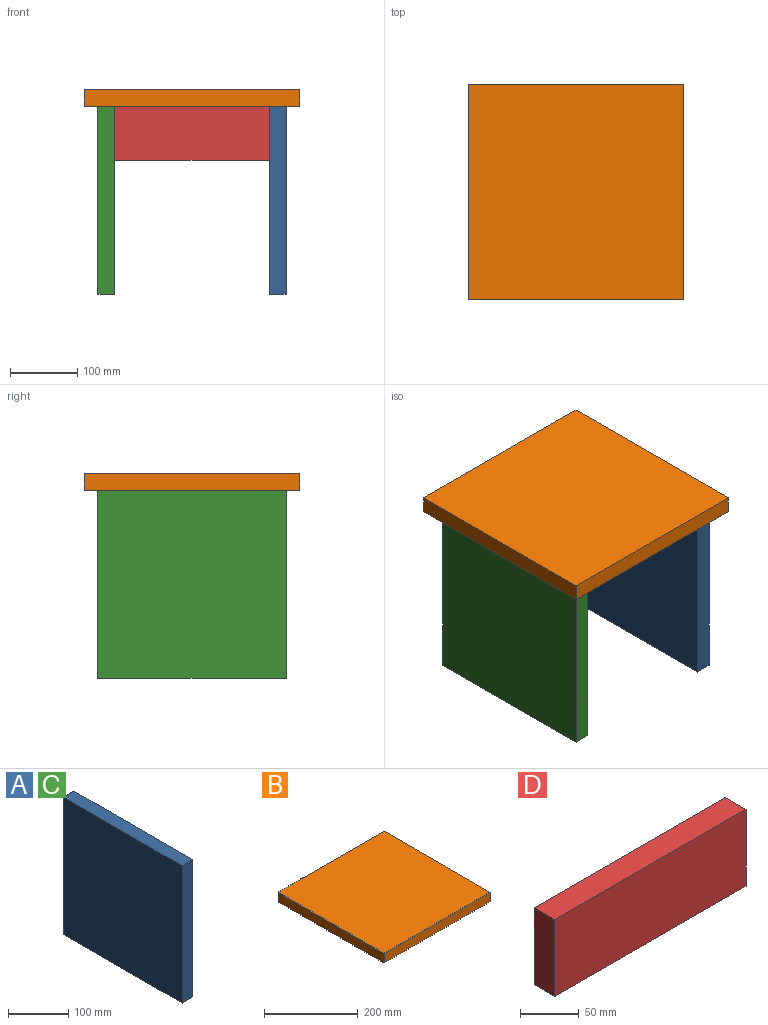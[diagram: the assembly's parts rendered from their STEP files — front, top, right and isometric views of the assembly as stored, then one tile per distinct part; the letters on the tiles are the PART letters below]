
ASSEMBLY  parts=4 mates=3
PART A: 6 faces, bbox 25x280x280 mm
  f0: plane 280x25mm, normal (0,0,1), area 7000mm2, adj f1,f3,f4,f5
  f1: plane 280x25mm, normal (0,-1,0), area 7000mm2, adj f0,f2,f4,f5
  f2: plane 280x25mm, normal (0,0,-1), area 7000mm2, adj f1,f3,f4,f5
  f3: plane 280x25mm, normal (0,1,0), area 7000mm2, adj f0,f2,f4,f5
  f4: plane 280x280mm, normal (1,0,0), area 78400mm2, adj f0,f1,f2,f3
  f5: plane 280x280mm, normal (-1,0,0), area 78400mm2, adj f0,f1,f2,f3
PART B: 6 faces, bbox 320x320x25 mm
  f0: plane 320x25mm, normal (-1,0,0), area 8000mm2, adj f1,f3,f4,f5
  f1: plane 320x25mm, normal (0,-1,0), area 8000mm2, adj f0,f2,f4,f5
  f2: plane 320x25mm, normal (1,0,0), area 8000mm2, adj f1,f3,f4,f5
  f3: plane 320x25mm, normal (0,1,0), area 8000mm2, adj f0,f2,f4,f5
  f4: plane 320x320mm, normal (0,0,1), area 102400mm2, adj f0,f1,f2,f3
  f5: plane 320x320mm, normal (0,0,-1), area 102400mm2, adj f0,f1,f2,f3
PART C: same geometry as A
PART D: 6 faces, bbox 230x25x80 mm
  f0: plane 230x25mm, normal (0,0,1), area 5750mm2, adj f1,f3,f4,f5
  f1: plane 80x25mm, normal (-1,0,0), area 2000mm2, adj f0,f2,f4,f5
  f2: plane 230x25mm, normal (0,0,-1), area 5750mm2, adj f1,f3,f4,f5
  f3: plane 80x25mm, normal (1,0,0), area 2000mm2, adj f0,f2,f4,f5
  f4: plane 230x80mm, normal (0,-1,0), area 18400mm2, adj f0,f1,f2,f3
  f5: plane 230x80mm, normal (0,1,0), area 18400mm2, adj f0,f1,f2,f3
PLACE A t=(327.07,-34.07,105.9)mm
PLACE B t=(52.07,-54.07,91.29)mm
PLACE C t=(72.07,-34.07,105.9)mm
PLACE D t=(39.49,118.43,106.75)mm
MATE fastened A.f0 <-> B.f5  axis (0,0,1) through (352.07,-34.07,91.29)mm
MATE fastened C.f0 <-> B.f5  axis (0,0,1) through (72.07,-34.07,91.29)mm
MATE fastened D.f1 <-> C.f4  axis (-1,0,0) through (97.07,105.93,91.29)mm
